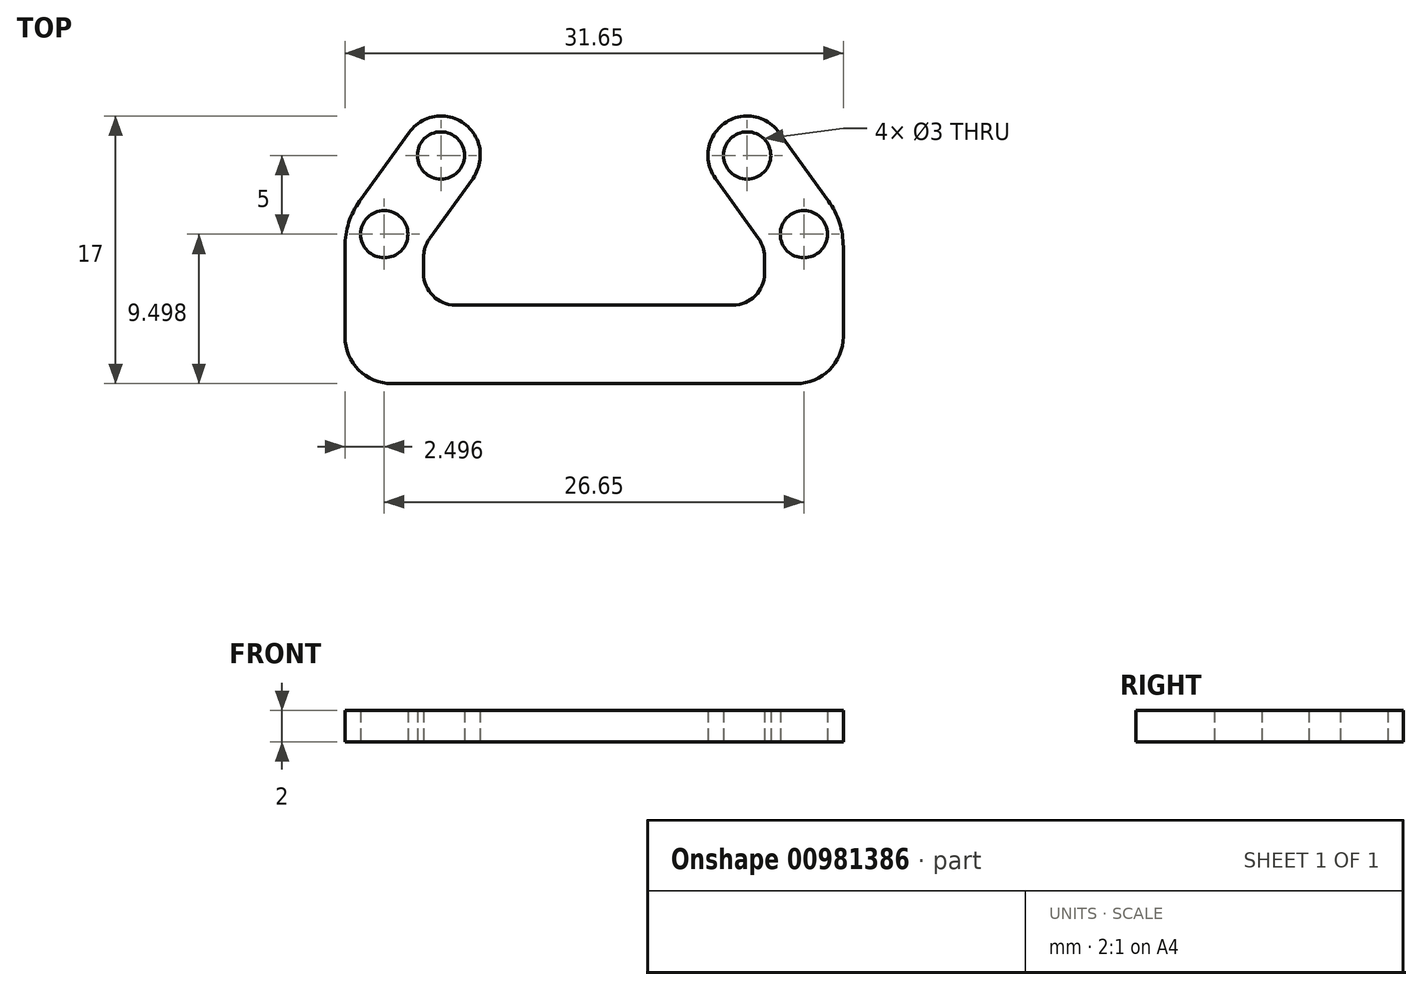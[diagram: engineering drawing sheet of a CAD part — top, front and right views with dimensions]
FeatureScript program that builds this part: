
annotation { "Feature Type Name" : "Feature", "Feature Type Description" : "" }
export const myFeature = defineFeature(function(context is Context, id is Id, definition is map)
    precondition{}
    {
        {
            var Q0;
            Q0=qCreatedBy(makeId("Top.planeOp"),FACE);
            var sketch = newSketch(context, id + "F0", { "sketchPlane" : qUnion([Q0])});
            skCircle(sketch, "E0", {"center": v(-30.64, 20.27) * mm, "radius": 1.5 * mm});
            skCircle(sketch, "E1", {"center": v(-27.04, 15.27) * mm, "radius": 1.5 * mm});
            skCircle(sketch, "E2.MirrorC", {"center": v(-53.7, 15.27) * mm, "radius": 1.5 * mm});
            skCircle(sketch, "E3.MirrorC", {"center": v(-50.1, 20.27) * mm, "radius": 1.5 * mm});
            skLineSegment(sketch, "E4", {"start": v(-53.2, 5.77) * mm, "end": v(-27.54, 5.77) * mm});
            skLineSegment(sketch, "E5", {"start": v(-55.25, 17.38) * mm, "end": v(-52.12, 21.73) * mm});
            skLineSegment(sketch, "E6", {"start": v(-56.2, 8.77) * mm, "end": v(-56.2, 14.46) * mm});
            skLineSegment(sketch, "E7", {"start": v(-24.54, 8.77) * mm, "end": v(-24.54, 14.46) * mm});
            skLineSegment(sketch, "E8.MirrorCS", {"start": v(-25.49, 17.38) * mm, "end": v(-28.62, 21.73) * mm});
            skLineSegment(sketch, "E9.0", {"start": v(-29.92, 14.98) * mm, "end": v(-32.67, 18.8) * mm});
            skLineSegment(sketch, "E10", {"start": v(-29.54, 13.82) * mm, "end": v(-29.54, 12.77) * mm});
            skLineSegment(sketch, "E11.MirrorCS", {"start": v(-50.82, 14.98) * mm, "end": v(-48.07, 18.8) * mm});
            skLineSegment(sketch, "E12.MirrorCS", {"start": v(-51.2, 13.82) * mm, "end": v(-51.2, 12.77) * mm});
            skLineSegment(sketch, "E13", {"start": v(-31.54, 10.77) * mm, "end": v(-49.2, 10.77) * mm});
            skArc(sketch, "E14", {"start": v(-48.07, 18.8) * mm, "mid": v(-48.63, 22.3) * mm, "end": v(-52.12, 21.73) * mm});
            skArc(sketch, "E15.MirrorCS", {"start": v(-32.67, 18.8) * mm, "mid": v(-32.1, 22.3) * mm, "end": v(-28.62, 21.73) * mm});
            skPoint(sketch, "E16.visualSharp", {"position": v(-56.2, 16.07) * mm});
            skArc(sketch, "E16.filletArc", {"start": v(-55.25, 17.38) * mm, "mid": v(-55.95, 16) * mm, "end": v(-56.2, 14.46) * mm});
            skPoint(sketch, "E17.visualSharp", {"position": v(-24.54, 16.07) * mm});
            skArc(sketch, "E17.filletArc", {"start": v(-24.54, 14.46) * mm, "mid": v(-24.79, 16) * mm, "end": v(-25.49, 17.38) * mm});
            skPoint(sketch, "E18.visualSharp", {"position": v(-56.2, 5.77) * mm});
            skArc(sketch, "E18.filletArc", {"start": v(-56.2, 8.77) * mm, "mid": v(-55.32, 6.65) * mm, "end": v(-53.2, 5.77) * mm});
            skPoint(sketch, "E19.visualSharp", {"position": v(-24.54, 5.77) * mm});
            skArc(sketch, "E19.filletArc", {"start": v(-27.54, 5.77) * mm, "mid": v(-25.42, 6.65) * mm, "end": v(-24.54, 8.77) * mm});
            skPoint(sketch, "E20.visualSharp", {"position": v(-29.54, 10.77) * mm});
            skArc(sketch, "E20.filletArc", {"start": v(-31.54, 10.77) * mm, "mid": v(-30.13, 11.35) * mm, "end": v(-29.54, 12.77) * mm});
            skPoint(sketch, "E21.visualSharp", {"position": v(-51.2, 10.77) * mm});
            skArc(sketch, "E21.filletArc", {"start": v(-51.2, 12.77) * mm, "mid": v(-50.6, 11.35) * mm, "end": v(-49.2, 10.77) * mm});
            skArc(sketch, "E22.filletArc", {"start": v(-50.82, 14.98) * mm, "mid": v(-51.1, 14.43) * mm, "end": v(-51.2, 13.82) * mm});
            skArc(sketch, "E23.filletArc", {"start": v(-29.54, 13.82) * mm, "mid": v(-29.64, 14.43) * mm, "end": v(-29.92, 14.98) * mm});
            skSolve(sketch);
        }
        {
            var Q0;
            Q0=makeQuery(id+"F0.imprint","IMPRINT",FACE,{"disambiguationData":[TD([[makeQuery(id+"F0.imprint","IMPRINT",EDGE,{"derivedFrom":sQuery(id+"F0.wireOp",EDGE,"E0")}),-1.0]])]});
            extrude(context, id + "F1", {"entities" : qUnion([Q0]), "depth" : 2 * mm, "offsetDistance" : 25 * mm});
        }
    });
